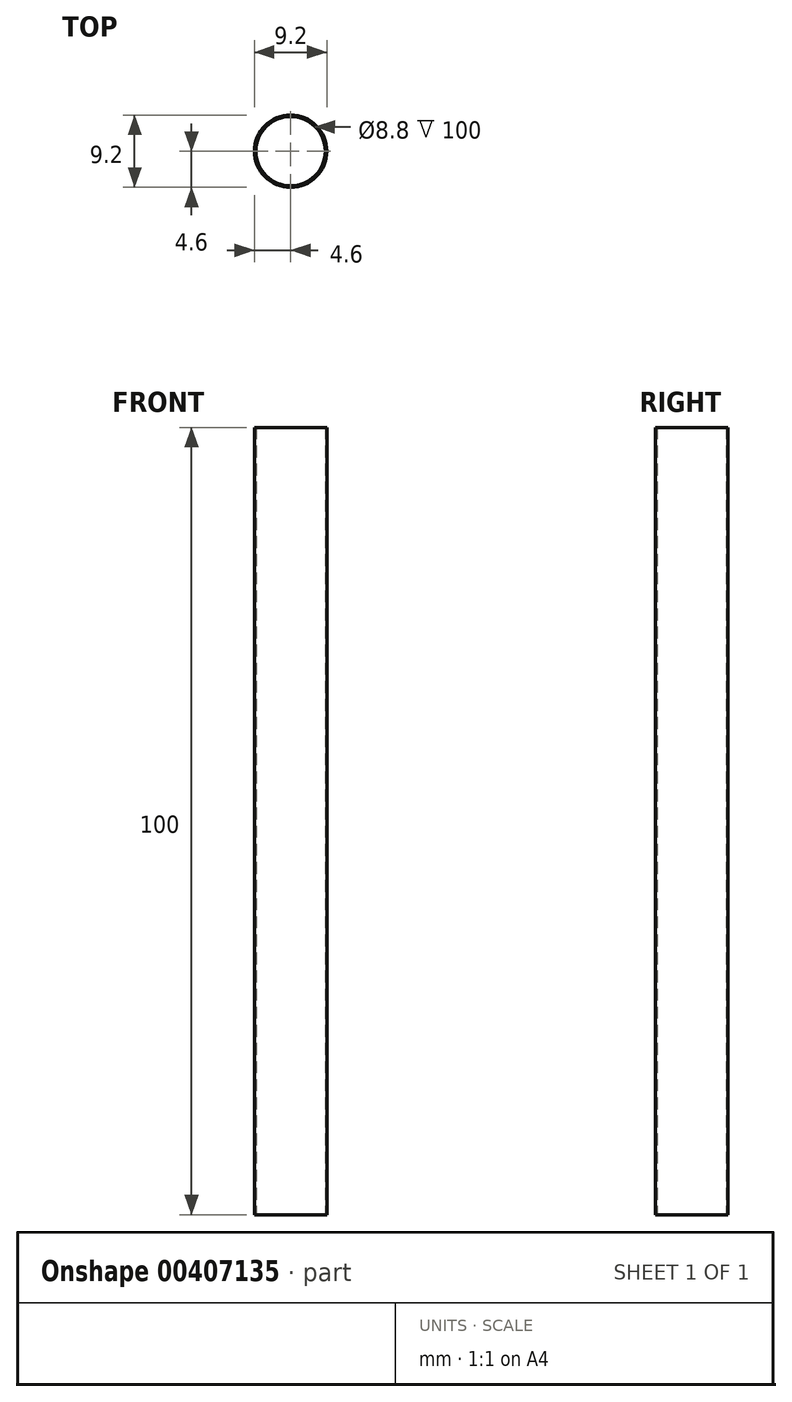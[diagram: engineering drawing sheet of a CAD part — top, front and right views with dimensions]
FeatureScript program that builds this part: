
annotation { "Feature Type Name" : "Feature", "Feature Type Description" : "" }
export const myFeature = defineFeature(function(context is Context, id is Id, definition is map)
    precondition{}
    {
        {
            var Q0;
            Q0=qCreatedBy(makeId("Top.planeOp"),FACE);
            var sketch = newSketch(context, id + "F0", { "sketchPlane" : qUnion([Q0])});
            skCircle(sketch, "E0", {"center": v(0, 0) * mm, "radius": 4.6 * mm});
            skCircle(sketch, "E1", {"center": v(0, 0) * mm, "radius": 4.4 * mm});
            skSolve(sketch);
        }
        {
            var Q0;
            Q0 = qSketchRegion(id + "F0", true);
            extrude(context, id + "F1", {"entities" : qUnion([Q0]), "depth" : 100 * mm});
        }
    });
